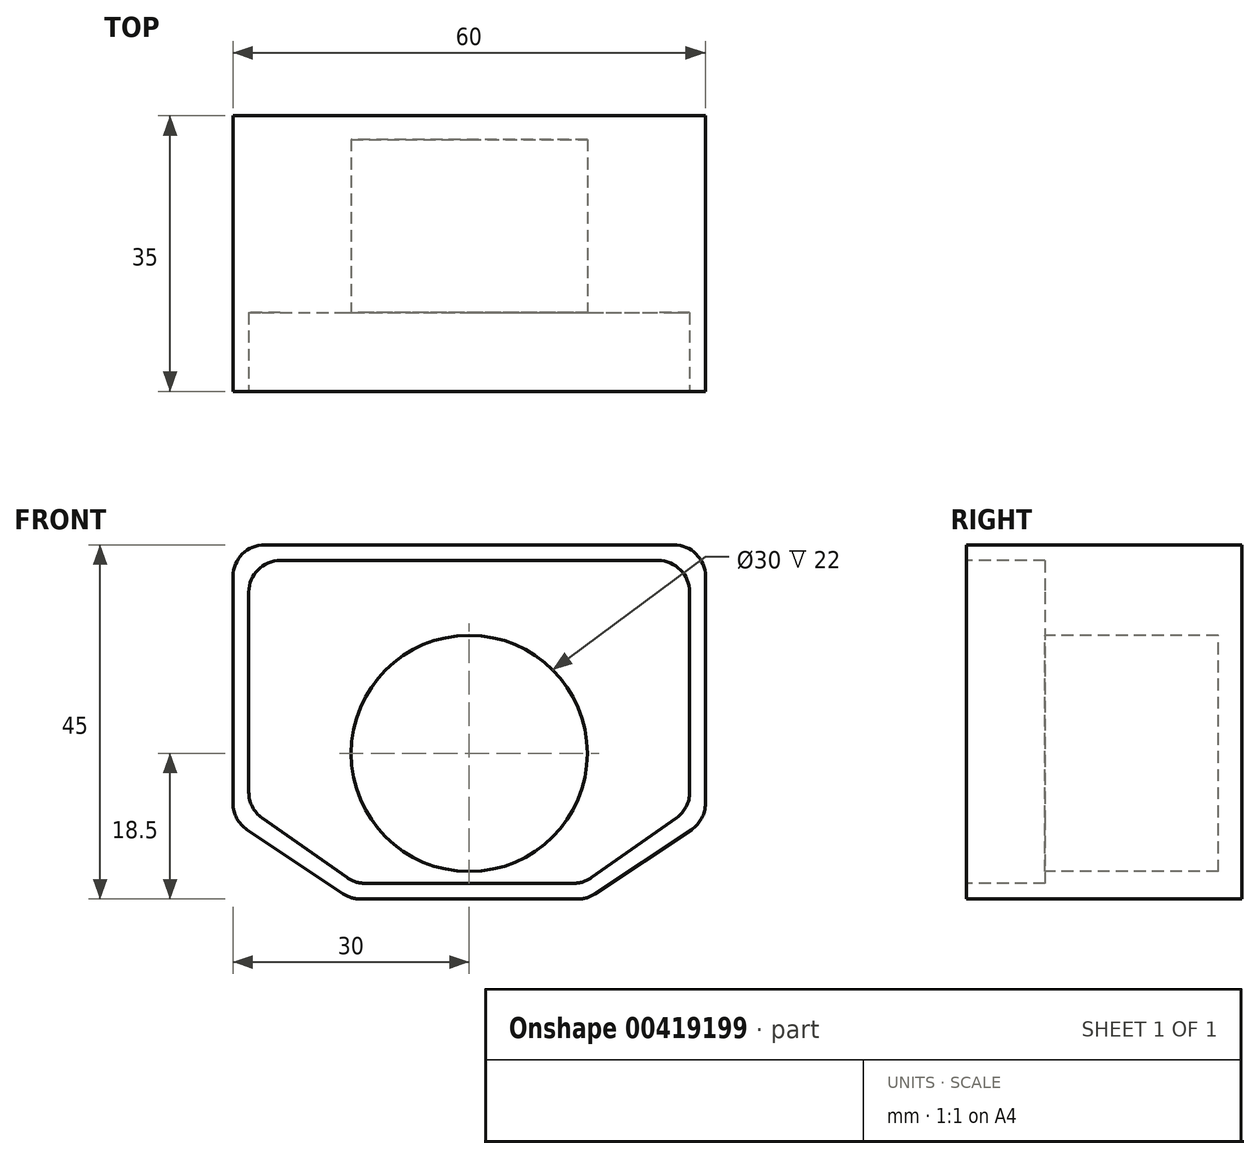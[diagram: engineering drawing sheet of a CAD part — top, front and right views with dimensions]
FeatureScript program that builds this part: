
annotation { "Feature Type Name" : "Feature", "Feature Type Description" : "" }
export const myFeature = defineFeature(function(context is Context, id is Id, definition is map)
    precondition{}
    {
        {
            var Q0;
            Q0=qCreatedBy(makeId("Front.planeOp"),FACE);
            var sketch = newSketch(context, id + "F0", { "sketchPlane" : qUnion([Q0])});
            skLineSegment(sketch, "E0.bottom", {"start": v(0, 0) * mm, "end": v(60, 0) * mm});
            skLineSegment(sketch, "E0.top", {"start": v(0, -45) * mm, "end": v(60, -45) * mm});
            skLineSegment(sketch, "E1", {"start": v(0, -45) * mm, "end": v(15, -45) * mm, "construction": true});
            skLineSegment(sketch, "E2", {"start": v(60, -45) * mm, "end": v(45, -45) * mm, "construction": true});
            skLineSegment(sketch, "E3", {"start": v(0, 0) * mm, "end": v(0, -35) * mm});
            skLineSegment(sketch, "E4", {"start": v(60, 0) * mm, "end": v(60, -35) * mm});
            skLineSegment(sketch, "E5", {"start": v(0, -35) * mm, "end": v(15, -45) * mm});
            skLineSegment(sketch, "E6", {"start": v(45, -45) * mm, "end": v(60, -35) * mm});
            skSolve(sketch);
        }
        {
            var Q0;
            Q0=qSketchRegion(id+"F0",true);
            extrude(context, id + "F1", {"entities" : qUnion([Q0]), "depth" : 35 * mm});
        }
        {
            var Q0;
            Q0=makeQuery(id+"F1.opExtrude","CAP_FACE",FACE,{"disambiguationData":[OSD([sQuery(id+"F0.wireOp",EDGE,"E0.bottom"),sQuery(id+"F0.wireOp",EDGE,"E0.top"),sQuery(id+"F0.wireOp",EDGE,"E0.left"),sQuery(id+"F0.wireOp",EDGE,"E0.right")])],"isStart":false});
            var sketch = newSketch(context, id + "F2", { "sketchPlane" : qUnion([Q0])});
            skLineSegment(sketch, "E7", {"start": v(0, 0) * mm, "end": v(0, -2) * mm, "construction": true});
            skLineSegment(sketch, "E8", {"start": v(0, -2) * mm, "end": v(2, -2) * mm, "construction": true});
            skLineSegment(sketch, "E9.bottom", {"start": v(2, -2) * mm, "end": v(58, -2) * mm});
            skLineSegment(sketch, "E10", {"start": v(2, -2) * mm, "end": v(2, -33.5) * mm});
            skLineSegment(sketch, "E11", {"start": v(58, -2) * mm, "end": v(58, -33.5) * mm});
            skLineSegment(sketch, "E12", {"start": v(30, -45) * mm, "end": v(30, -43) * mm, "construction": true});
            skLineSegment(sketch, "E13", {"start": v(30, -43) * mm, "end": v(30, -26.5) * mm, "construction": true});
            skCircle(sketch, "E14", {"center": v(30, -26.5) * mm, "radius": 15 * mm});
            skLineSegment(sketch, "E15", {"start": v(30, -43) * mm, "end": v(15.5, -43) * mm});
            skLineSegment(sketch, "E16", {"start": v(30, -43) * mm, "end": v(44.5, -43) * mm});
            skLineSegment(sketch, "E17", {"start": v(2, -33.5) * mm, "end": v(15.5, -43) * mm});
            skLineSegment(sketch, "E18", {"start": v(44.5, -43) * mm, "end": v(58, -33.5) * mm});
            skSolve(sketch);
        }
        {
            var Q0;
            Q0=makeQuery(id+"F2.imprint","IMPRINT",FACE,{"disambiguationData":[TD([[makeQuery(id+"F2.imprint","IMPRINT",EDGE,{"derivedFrom":sQuery(id+"F2.wireOp",EDGE,"E9.bottom")}),-1.0]])]});
            extrude(context, id + "F3", {"entities" : qUnion([Q0]), "operationType" : NewBodyOperationType.REMOVE, "oppositeDirection" : true, "depth" : 10 * mm});
        }
        {
            var Q0;
            Q0=makeQuery(id+"F3.boolean.opBoolean","SPLIT",FACE,{"disambiguationData":[TD([makeQuery(id+"F3.opExtrude","SWEPT_FACE",FACE,{"disambiguationData":[OSD([sQuery(id+"F2.wireOp",EDGE,"O5j804fB-8yol-YFvD-zu38-NWGoYmatLYKw")])]})])],"derivedFrom":makeQuery(id+"F1.opExtrude","CAP_FACE",FACE,{"disambiguationData":[OSD([sQuery(id+"F0.wireOp",EDGE,"E0.bottom"),sQuery(id+"F0.wireOp",EDGE,"E0.top"),sQuery(id+"F0.wireOp",EDGE,"E0.left"),sQuery(id+"F0.wireOp",EDGE,"E0.right")])],"isStart":false})});
            var Q1;
            Q1=makeQuery(id+"F3.boolean.opBoolean","SPLIT",FACE,{"disambiguationData":[TD([makeQuery(id+"F3.opExtrude","SWEPT_FACE",FACE,{"disambiguationData":[OSD([sQuery(id+"F2.wireOp",EDGE,"E14")])]})])],"derivedFrom":makeQuery(id+"F1.opExtrude","CAP_FACE",FACE,{"disambiguationData":[OSD([sQuery(id+"F0.wireOp",EDGE,"E0.bottom"),sQuery(id+"F0.wireOp",EDGE,"E0.top"),sQuery(id+"F0.wireOp",EDGE,"E3"),sQuery(id+"F0.wireOp",EDGE,"E4"),sQuery(id+"F0.wireOp",EDGE,"PvXtP6X7-4Lpo-MaVH-79Q1-9Lcm4Y1i0ssL"),sQuery(id+"F0.wireOp",EDGE,"bQJBMBWi-5KoV-E722-KKUO-etTEZJzEf8hp")])],"isStart":false})});
            extrude(context, id + "F4", {"entities" : qUnion([Q0, Q1]), "operationType" : NewBodyOperationType.REMOVE, "oppositeDirection" : true, "depth" : 32 * mm});
        }
        {
            var Q0;
            Q0=makeQuery(id+"F1.opExtrude","SWEPT_EDGE",EDGE,{"disambiguationData":[OSD([sQuery(id+"F0.wireOp",EDGE,"E0.bottom"),sQuery(id+"F0.wireOp",EDGE,"E4")])]});
            var Q1;
            Q1=makeQuery(id+"F1.opExtrude","SWEPT_EDGE",EDGE,{"disambiguationData":[OSD([sQuery(id+"F0.wireOp",EDGE,"E4"),sQuery(id+"F0.wireOp",EDGE,"E6")])]});
            var Q2;
            Q2=makeQuery(id+"F1.opExtrude","SWEPT_EDGE",EDGE,{"disambiguationData":[OSD([sQuery(id+"F0.wireOp",EDGE,"E0.bottom"),sQuery(id+"F0.wireOp",EDGE,"E3")])]});
            var Q3;
            Q3=makeQuery(id+"F1.opExtrude","SWEPT_EDGE",EDGE,{"disambiguationData":[OSD([sQuery(id+"F0.wireOp",EDGE,"E0.top"),sQuery(id+"F0.wireOp",EDGE,"E6")])]});
            var Q4;
            Q4=makeQuery(id+"F1.opExtrude","SWEPT_EDGE",EDGE,{"disambiguationData":[OSD([sQuery(id+"F0.wireOp",EDGE,"E0.top"),sQuery(id+"F0.wireOp",EDGE,"E5")])]});
            var Q5;
            Q5=makeQuery(id+"F1.opExtrude","SWEPT_EDGE",EDGE,{"disambiguationData":[OSD([sQuery(id+"F0.wireOp",EDGE,"E3"),sQuery(id+"F0.wireOp",EDGE,"E5")])]});
            var Q6;
            Q6=makeQuery(id+"F3.boolean.opBoolean","COPY",EDGE,{"derivedFrom":makeQuery(id+"F3.opExtrude","SWEPT_EDGE",EDGE,{"disambiguationData":[OSD([sQuery(id+"F2.wireOp",EDGE,"E10"),sQuery(id+"F2.wireOp",EDGE,"E17")])]})});
            var Q7;
            Q7=makeQuery(id+"F3.boolean.opBoolean","COPY",EDGE,{"derivedFrom":makeQuery(id+"F3.opExtrude","SWEPT_EDGE",EDGE,{"disambiguationData":[OSD([sQuery(id+"F2.wireOp",EDGE,"E16"),sQuery(id+"F2.wireOp",EDGE,"E18")])]})});
            var Q8;
            Q8=makeQuery(id+"F3.boolean.opBoolean","COPY",EDGE,{"derivedFrom":makeQuery(id+"F3.opExtrude","SWEPT_EDGE",EDGE,{"disambiguationData":[OSD([sQuery(id+"F2.wireOp",EDGE,"E15"),sQuery(id+"F2.wireOp",EDGE,"E17")])]})});
            var Q9;
            Q9=makeQuery(id+"F3.boolean.opBoolean","COPY",EDGE,{"derivedFrom":makeQuery(id+"F3.opExtrude","SWEPT_EDGE",EDGE,{"disambiguationData":[OSD([sQuery(id+"F2.wireOp",EDGE,"E11"),sQuery(id+"F2.wireOp",EDGE,"E18")])]})});
            var Q10;
            Q10=makeQuery(id+"F3.boolean.opBoolean","COPY",EDGE,{"derivedFrom":makeQuery(id+"F3.opExtrude","SWEPT_EDGE",EDGE,{"disambiguationData":[OSD([sQuery(id+"F2.wireOp",EDGE,"E9.bottom"),sQuery(id+"F2.wireOp",EDGE,"E11")])]})});
            var Q11;
            Q11=makeQuery(id+"F3.boolean.opBoolean","COPY",EDGE,{"derivedFrom":makeQuery(id+"F3.opExtrude","SWEPT_EDGE",EDGE,{"disambiguationData":[OSD([sQuery(id+"F2.wireOp",EDGE,"E9.bottom"),sQuery(id+"F2.wireOp",EDGE,"E10")])]})});
            fillet(context, id + "F5", {"entities" : qUnion([Q0, Q1, Q2, Q3, Q4, Q5, Q6, Q7, Q8, Q9, Q10, Q11]), "radius" : 4 * mm, "tangentPropagation" : true, "allowEdgeOverflow" : false});
        }
    });
